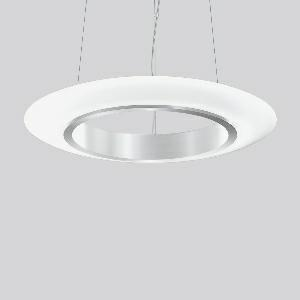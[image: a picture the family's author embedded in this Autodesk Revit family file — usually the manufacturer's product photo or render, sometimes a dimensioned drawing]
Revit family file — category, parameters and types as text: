
# Revit family: ring_of_fire_p_312546_004_1_730_3149
name_source: partatom
category: Lighting Fixtures
units: mm (PartAtom-declared; Revit-internal decimal feet)

## family parameters
Cut with Voids When Loaded = No
Host = Face
Light Source = No
Part Type = Normal
Room Calculation Point = No
Round Connector Dimension = Use Diameter
Shared = No

## types (1)
- RING OF FIRE P (1 x LED Modul 840, 5800 lm, 4000)
    Apparent Load = 71 VA
    CIE Flux Codes = 43 72 90 52 100
    Color Rendering = 80
    Color Temperature = 4000
    Default Elevation = 1800 mm
    Description = Series: RING OF FIRE
A uniquely shaped pendant luminaire with elliptical glass. Supporting ring made of anodised aluminium. Canopy aluminium anodised. Opal glass: mouth-blown, satin finish. Suitable for pendant. 3-point steel cable suspension, steplessly adjustable. Special lengths available on request. 
Colour: anodised aluminium
Diameter: 690 mm
Height: 81 mm
Suspension length: 500-1200 mm
Lamp: LED
Socket: without socket
Colour temperature: 4000K
Colour rendering index (CRI): 80
System power: 71 W
Rated luminous flux: 5800 lm
Luminous efficiency: 82 lm/W
Control gear: Dimmable Bluetooth converter
Protection class: I
Type of protection: IP 20
    Height = 81 mm
    Lamp = 1 x LED Modul 840
    Lamp Light Flux = 5800 lm
    Lamp count = 1
    Length = 690 mm
    Lifetime = 50000 h
    Luminous efficacy = 82 lm/W
    Manufacturer = RZB
    ModVariant = No
    Model = 312546.004.1.730
    Mounting Place = Ceiling
    Mounting Type = Pendant
    Number of Poles = 1
    OnlyDefault = Yes
    Power Factor = 1
    Product Name = RING OF FIRE P
    Product group = Pendant luminaires
    ProductGroupID = 902
    Protection Class = Protection class I
    Protection Degree = IP 20
    RLX_Detail_Level = 1
    RLX_Emergency_Light_Flux = 0 lm
    RLX_Emergency_Type = 0
    RLX_Emergency_Type_DB = No
    RlxData = <blob elided: 30381 chars, md5=481cb62d>
    Socket = socket
    Standby Power = 0 W
    System Light Flux = 5800 lm
    System Power = 71 W
    Type Comments = Product without accessories
    Type Image = 311570.004.jpg
    URL = http://relux.com
    VarID = ---
    Voltage = 230 V
    Voltage Range = 220-240 V
    Weight = 0.00 kg
    Width = 0 mm  [stored 0 ft]

note: [stored X ft] marks values corroborated as IEEE doubles in the binary element streams (Revit-internal decimal feet)

## geometry (parser evidence)
native form markers: Blend x4, Sweep x10
no freeform markers — native parametric forms only
